# Revit family: Seat-LaZBoy-Assymble_Lounge_Seating-AS32L
name_source: partatom
category: Furniture
revit_build: Autodesk Revit 2017 (Build: 20160225_1515(x64)
units: mm (PartAtom-declared; Revit-internal decimal feet)

## family parameters
Always vertical = Yes
Cut with Voids When Loaded = No
OmniClass Number = 23.40.20.00
OmniClass Title = General Furniture and Specialties
Room Calculation Point = No
Shared = No
Work Plane-Based = No

## types (4) — shared parameters
Assembly Code = E2020200
Depth = 30.75"
Height = 32.75"
Manufacturer = LaZBoy
Product Documentation Link = URL
URL = https://www.la-z-boy.com
Width = 75.00"

## per-type parameters (varying)
| type | Description | Model |
| Upholstered Arms | 3 Seat Lounge Chair, Left Side Facing with Upholstered Arms | AS32LF |
| Urethane Arms Caps | 3 Seat Lounge Chair, Left Side Facing with Urethane Arms Caps | AS32LU |
| Wood Arms Caps | 3 Seat Lounge Chair, Left Side Facing with Wood Arms Caps | AS32LW |
| Solid Surface Arms Caps | 3 Seat Lounge Chair, Left Side Facing with Solid Surface Arms Caps | AS32LJ |

## geometry (parser evidence)
native form markers: Sweep x5
no freeform markers — native parametric forms only
